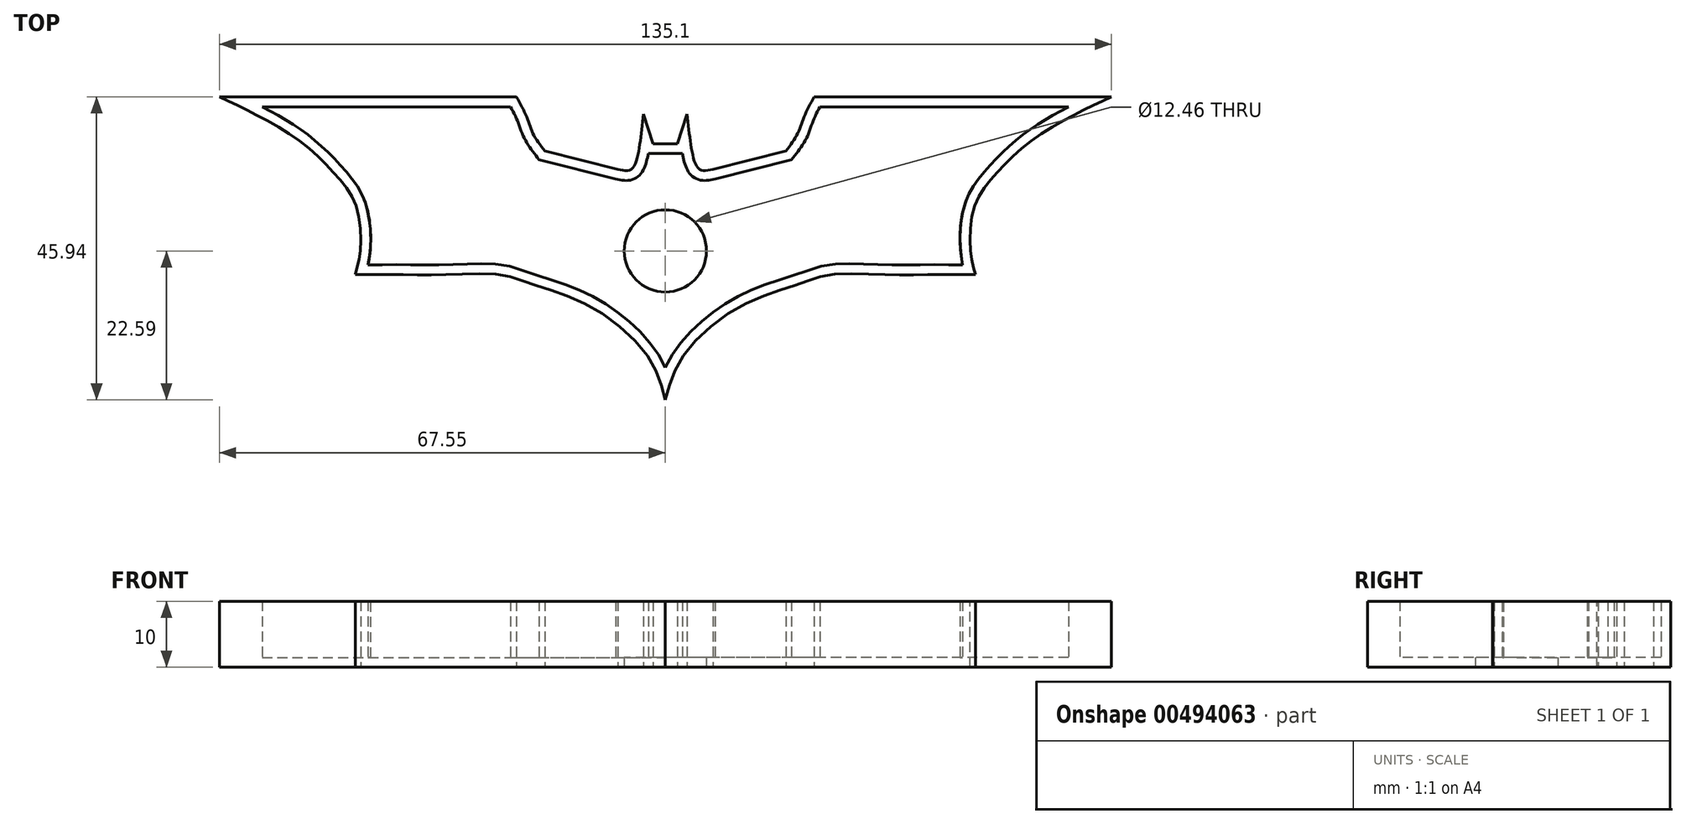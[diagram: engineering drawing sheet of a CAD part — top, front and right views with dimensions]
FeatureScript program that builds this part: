
annotation { "Feature Type Name" : "Feature", "Feature Type Description" : "" }
export const myFeature = defineFeature(function(context is Context, id is Id, definition is map)
    precondition{}
    {
        {
            var Q0;
            Q0=qCreatedBy(makeId("Top.planeOp"),FACE);
            var sketch = newSketch(context, id + "F0", { "sketchPlane" : qUnion([Q0])});
            skLineSegment(sketch, "E0", {"start": v(-67.55, 23.35) * mm, "end": v(-22.54, 23.35) * mm});
            skLineSegment(sketch, "E1", {"start": v(-3.31, 20.75) * mm, "end": v(-1.83, 16.25) * mm});
            skLineSegment(sketch, "E2", {"start": v(-18.25, 15.14) * mm, "end": v(-7.2, 12.35) * mm});
            skFitSpline(sketch, "E3", {"points": [v(-67.55, 23.35) * mm, v(-62.24, 20.78) * mm, v(-55.06, 16.42) * mm, v(-49.92, 11.54) * mm, v(-46.84, 6.8) * mm, v(-46.2, 0) * mm, v(-46.97, -3.6) * mm], "startDerivative": vector(31.05, -14.46) * mm, "endDerivative": vector(-7.3, -24.9) * mm});
            skFitSpline(sketch, "E4", {"points": [v(-46.97, -3.6) * mm, v(-44.54, -3.6) * mm, v(-38.76, -3.6) * mm, v(-32.99, -3.6) * mm, v(-25.03, -3.6) * mm, v(-19.9, -5.14) * mm, v(-11.95, -8.09) * mm, v(-2.7, -15.92) * mm, v(0, -22.59) * mm], "startDerivative": vector(28.24, -0.06) * mm, "endDerivative": vector(13.13, -50.64) * mm});
            skFitSpline(sketch, "E5", {"points": [v(-22.54, 23.35) * mm, v(-21, 20.27) * mm, v(-20.02, 17.74) * mm, v(-18.25, 15.14) * mm], "startDerivative": vector(4.9, -8.9) * mm, "endDerivative": vector(5.94, -7.66) * mm});
            skFitSpline(sketch, "E6", {"points": [v(-7.2, 12.35) * mm, v(-5.2, 12.35) * mm, v(-4.03, 15.14) * mm, v(-3.31, 20.75) * mm], "startDerivative": vector(8.67, -1.9) * mm, "endDerivative": vector(1.4, 13.57) * mm});
            skFitSpline(sketch, "E7", {"points": [v(-1.83, 16.25) * mm, v(0, 16.25) * mm], "startDerivative": vector(1.83, 0) * mm, "endDerivative": vector(1.83, 0) * mm});
            skFitSpline(sketch, "E8.MirrorCS", {"points": [v(1.83, 16.25) * mm, v(0, 16.25) * mm], "startDerivative": vector(-1.83, 0) * mm, "endDerivative": vector(-1.83, 0) * mm});
            skLineSegment(sketch, "E9.MirrorCS", {"start": v(3.31, 20.75) * mm, "end": v(1.83, 16.25) * mm});
            skFitSpline(sketch, "E10.MirrorCS", {"points": [v(22.54, 23.35) * mm, v(21, 20.27) * mm, v(20.02, 17.74) * mm, v(18.25, 15.14) * mm], "startDerivative": vector(-4.9, -8.9) * mm, "endDerivative": vector(-5.94, -7.66) * mm});
            skFitSpline(sketch, "E11.MirrorCS", {"points": [v(7.2, 12.35) * mm, v(5.2, 12.35) * mm, v(4.03, 15.14) * mm, v(3.31, 20.75) * mm], "startDerivative": vector(-8.67, -1.9) * mm, "endDerivative": vector(-1.4, 13.57) * mm});
            skFitSpline(sketch, "E12.MirrorCS", {"points": [v(46.97, -3.6) * mm, v(44.54, -3.6) * mm, v(38.76, -3.6) * mm, v(32.99, -3.6) * mm, v(25.03, -3.6) * mm, v(19.9, -5.14) * mm, v(11.95, -8.09) * mm, v(2.7, -15.92) * mm, v(0, -22.59) * mm], "startDerivative": vector(-28.24, -0.06) * mm, "endDerivative": vector(-13.13, -50.64) * mm});
            skFitSpline(sketch, "E13.MirrorCS", {"points": [v(67.55, 23.35) * mm, v(62.24, 20.78) * mm, v(55.06, 16.42) * mm, v(49.92, 11.54) * mm, v(46.84, 6.8) * mm, v(46.2, 0) * mm, v(46.97, -3.6) * mm], "startDerivative": vector(-31.05, -14.46) * mm, "endDerivative": vector(7.3, -24.9) * mm});
            skLineSegment(sketch, "E14.MirrorCS", {"start": v(18.25, 15.14) * mm, "end": v(7.2, 12.35) * mm});
            skLineSegment(sketch, "E15.MirrorCS", {"start": v(67.55, 23.35) * mm, "end": v(22.54, 23.35) * mm});
            skSolve(sketch);
        }
        {
            var Q0;
            Q0=makeQuery(id+"F0.imprint","IMPRINT",FACE,{"disambiguationData":[TD([[makeQuery(id+"F0.imprint","IMPRINT",EDGE,{"derivedFrom":sQuery(id+"F0.wireOp",EDGE,"E0")}),-1.0]])]});
            extrude(context, id + "F1", {"entities" : qUnion([Q0]), "depth" : 10 * mm});
        }
        {
            var Q0;
            Q0=makeQuery(id+"F1.opExtrude","CAP_FACE",FACE,{"disambiguationData":[OSD([sQuery(id+"F0.wireOp",EDGE,"E0"),sQuery(id+"F0.wireOp",EDGE,"E1"),sQuery(id+"F0.wireOp",EDGE,"E2"),sQuery(id+"F0.wireOp",EDGE,"E3"),sQuery(id+"F0.wireOp",EDGE,"E4"),sQuery(id+"F0.wireOp",EDGE,"E5"),sQuery(id+"F0.wireOp",EDGE,"E6"),sQuery(id+"F0.wireOp",EDGE,"E7"),sQuery(id+"F0.wireOp",EDGE,"E8.MirrorCS"),sQuery(id+"F0.wireOp",EDGE,"E9.MirrorCS"),sQuery(id+"F0.wireOp",EDGE,"E10.MirrorCS"),sQuery(id+"F0.wireOp",EDGE,"E11.MirrorCS"),sQuery(id+"F0.wireOp",EDGE,"E12.MirrorCS"),sQuery(id+"F0.wireOp",EDGE,"E13.MirrorCS"),sQuery(id+"F0.wireOp",EDGE,"E14.MirrorCS"),sQuery(id+"F0.wireOp",EDGE,"E15.MirrorCS")])],"isStart":false});
            shell(context, id + "F2", {"entities" : qUnion([Q0]), "thickness" : 1.5 * mm});
        }
        {
            var Q0;
            Q0=makeQuery(id+"F1.opExtrude","CAP_FACE",FACE,{"disambiguationData":[OSD([sQuery(id+"F0.wireOp",EDGE,"E0"),sQuery(id+"F0.wireOp",EDGE,"E1"),sQuery(id+"F0.wireOp",EDGE,"E2"),sQuery(id+"F0.wireOp",EDGE,"E3"),sQuery(id+"F0.wireOp",EDGE,"E4"),sQuery(id+"F0.wireOp",EDGE,"E5"),sQuery(id+"F0.wireOp",EDGE,"E6"),sQuery(id+"F0.wireOp",EDGE,"E7"),sQuery(id+"F0.wireOp",EDGE,"E8.MirrorCS"),sQuery(id+"F0.wireOp",EDGE,"E9.MirrorCS"),sQuery(id+"F0.wireOp",EDGE,"E10.MirrorCS"),sQuery(id+"F0.wireOp",EDGE,"E11.MirrorCS"),sQuery(id+"F0.wireOp",EDGE,"E12.MirrorCS"),sQuery(id+"F0.wireOp",EDGE,"E13.MirrorCS"),sQuery(id+"F0.wireOp",EDGE,"E14.MirrorCS"),sQuery(id+"F0.wireOp",EDGE,"E15.MirrorCS")])],"isStart":true});
            var sketch = newSketch(context, id + "F3", { "sketchPlane" : qUnion([Q0])});
            skCircle(sketch, "E16", {"center": v(0, 0) * mm, "radius": 6.23 * mm});
            skSolve(sketch);
        }
        {
            var Q0;
            Q0 = qSketchRegion(id + "F3", true);
            extrude(context, id + "F4", {"entities" : qUnion([Q0]), "operationType" : NewBodyOperationType.REMOVE, "oppositeDirection" : true, "depth" : 25 * mm});
        }
    });
